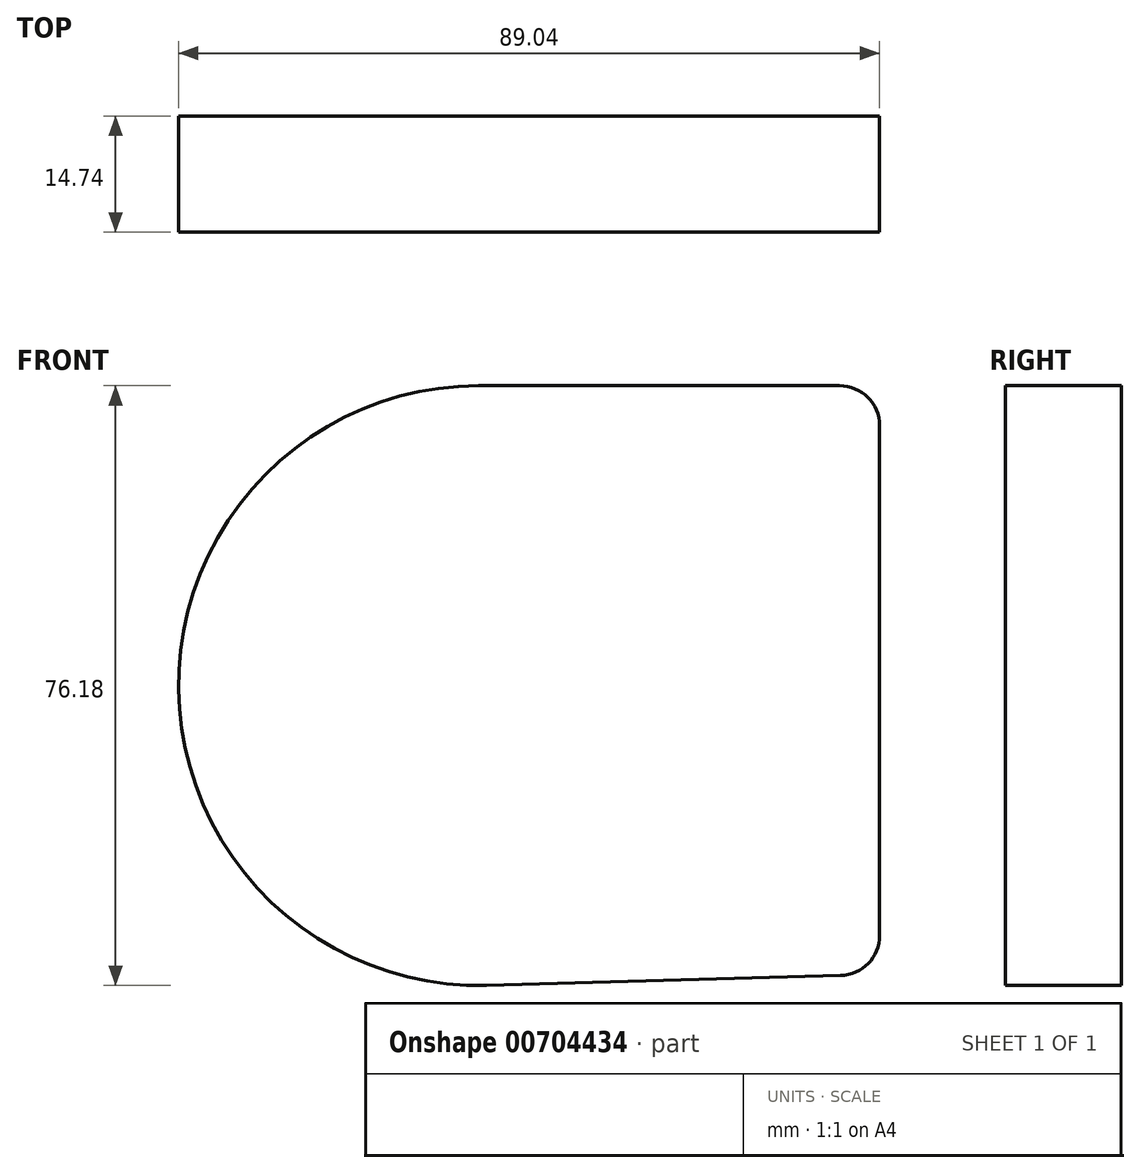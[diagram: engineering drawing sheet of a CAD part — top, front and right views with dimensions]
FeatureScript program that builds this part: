
annotation { "Feature Type Name" : "Feature", "Feature Type Description" : "" }
export const myFeature = defineFeature(function(context is Context, id is Id, definition is map)
    precondition{}
    {
        {
            var Q0;
            Q0=qCreatedBy(makeId("Front.planeOp"),FACE);
            var sketch = newSketch(context, id + "F0", { "sketchPlane" : qUnion([Q0])});
            skCircle(sketch, "E0", {"center": v(0, 0) * mm, "radius": 38.1 * mm});
            skLineSegment(sketch, "E1", {"start": v(0, 38.1) * mm, "end": v(50.95, 38.1) * mm});
            skLineSegment(sketch, "E2", {"start": v(50.95, 38.1) * mm, "end": v(50.95, -36.71) * mm});
            skLineSegment(sketch, "E3", {"start": v(50.95, -36.71) * mm, "end": v(0, -38.1) * mm});
            skSolve(sketch);
        }
        {
            var Q0;
            Q0=sQuery(id+"F0.wireOp",EDGE,"E0");
            extrude(context, id + "F1", {"bodyType" : ToolBodyType.SURFACE, "surfaceEntities" : qUnion([Q0]), "endBound" : BoundingType.SYMMETRIC, "depth" : 34.54 * mm, "offsetDistance" : 25.4 * mm});
        }
        {
            var Q0;
            Q0 = qSketchRegion(id + "F0", true);
            extrude(context, id + "F2", {"entities" : qUnion([Q0]), "endBound" : BoundingType.SYMMETRIC, "depth" : 14.73 * mm, "offsetDistance" : 25.4 * mm});
        }
        {
            var Q0;
            Q0=makeQuery(id+"F2.opExtrude","SWEPT_EDGE",EDGE,{"disambiguationData":[OSD([sQuery(id+"F0.wireOp",EDGE,"E1"),sQuery(id+"F0.wireOp",EDGE,"E2")])]});
            var Q1;
            Q1=makeQuery(id+"F2.opExtrude","SWEPT_EDGE",EDGE,{"disambiguationData":[OSD([sQuery(id+"F0.wireOp",EDGE,"E2"),sQuery(id+"F0.wireOp",EDGE,"E3")])]});
            var Q2;
            Q2=makeQuery(id+"F2.opExtrude","SWEPT_EDGE",EDGE,{"disambiguationData":[OSD([sQuery(id+"F0.wireOp",EDGE,"E0"),sQuery(id+"F0.wireOp",EDGE,"E3")])]});
            fillet(context, id + "F3", {"entities" : qUnion([Q0, Q1, Q2]), "radius" : 5.08 * mm, "tangentPropagation" : true, "allowEdgeOverflow" : false});
        }
    });
